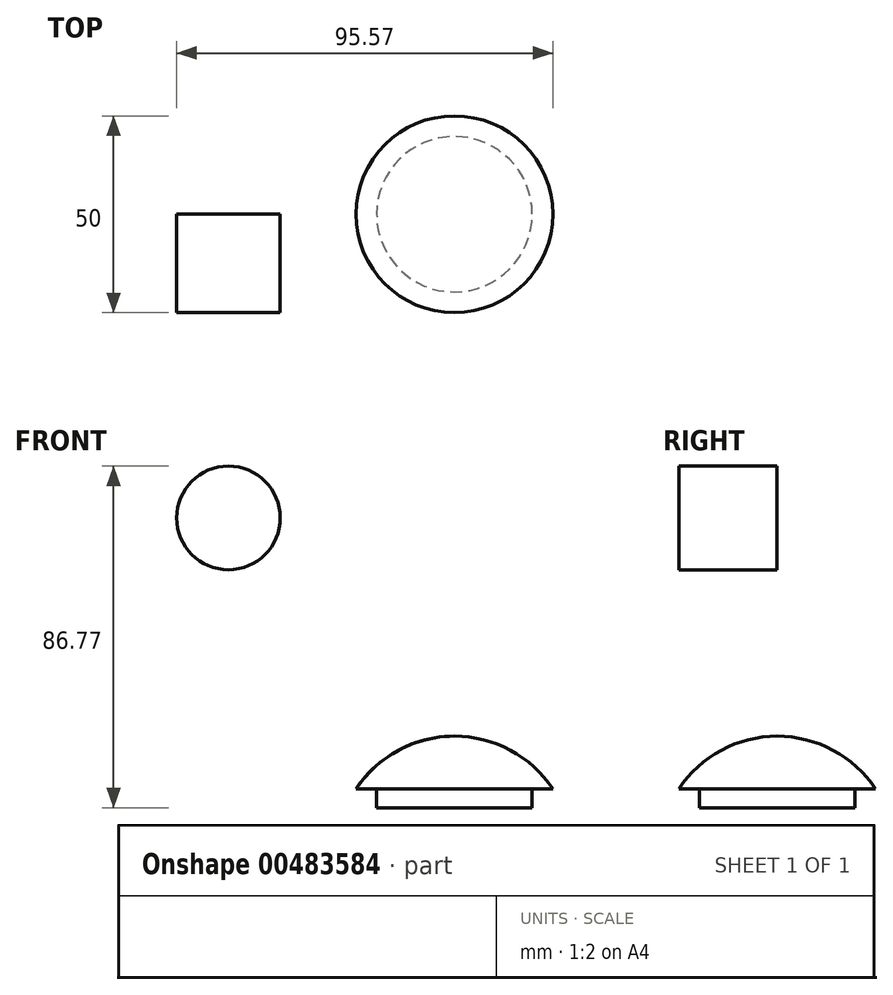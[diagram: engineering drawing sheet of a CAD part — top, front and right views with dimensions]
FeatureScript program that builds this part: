
annotation { "Feature Type Name" : "Feature", "Feature Type Description" : "" }
export const myFeature = defineFeature(function(context is Context, id is Id, definition is map)
    precondition{}
    {
        {
            var Q0;
            Q0=qCreatedBy(makeId("Top.planeOp"),FACE);
            var sketch = newSketch(context, id + "F0", { "sketchPlane" : qUnion([Q0])});
            skCircle(sketch, "E0", {"center": v(0, 0) * mm, "radius": 19.75 * mm});
            skSolve(sketch);
        }
        {
            var Q0;
            Q0=makeQuery(id+"F0.imprint","IMPRINT",FACE,{"disambiguationData":[TD([[makeQuery(id+"F0.imprint","IMPRINT",EDGE,{"derivedFrom":sQuery(id+"F0.wireOp",EDGE,"E0")}),1.0]])]});
            extrude(context, id + "F1", {"entities" : qUnion([Q0]), "oppositeDirection" : true, "depth" : 4.75 * mm});
        }
        {
            var Q0;
            Q0=qCreatedBy(makeId("Front.planeOp"),FACE);
            var sketch = newSketch(context, id + "F2", { "sketchPlane" : qUnion([Q0])});
            skLineSegment(sketch, "E1", {"start": v(0, 0) * mm, "end": v(-25, 0) * mm});
            skArc(sketch, "E2", {"start": v(0, 13.42) * mm, "mid": v(-14.19, 9.85) * mm, "end": v(-25, 0) * mm});
            skLineSegment(sketch, "E3", {"start": v(0, 13.42) * mm, "end": v(0, 0) * mm});
            skLineSegment(sketch, "E4", {"start": v(0, 13.42) * mm, "end": v(16.84, 13.42) * mm, "construction": true});
            skSolve(sketch);
        }
        {
            var Q0;
            Q0=makeQuery(id+"F2.imprint","IMPRINT",FACE,{"disambiguationData":[TD([[makeQuery(id+"F2.imprint","IMPRINT",EDGE,{"derivedFrom":sQuery(id+"F2.wireOp",EDGE,"E1")}),-1.0]])]});
            var Q1;
            Q1=sQuery(id+"F2.wireOp",EDGE,"E3");
            revolve(context, id + "F3", {"operationType" : NewBodyOperationType.ADD, "entities" : qUnion([Q0]), "axis" : qUnion([Q1]), "revolveType" : RevolveType.FULL});
        }
        {
            var Q0;
            Q0=qCreatedBy(makeId("Front.planeOp"),FACE);
            var sketch = newSketch(context, id + "F4", { "sketchPlane" : qUnion([Q0])});
            skCircle(sketch, "E5", {"center": v(-57.42, 68.86) * mm, "radius": 13.16 * mm});
            skSolve(sketch);
        }
        {
            var Q0;
            Q0=makeQuery(id+"F4.imprint","IMPRINT",FACE,{"disambiguationData":[TD([[makeQuery(id+"F4.imprint","IMPRINT",EDGE,{"derivedFrom":sQuery(id+"F4.wireOp",EDGE,"E5")}),1.0]])]});
            extrude(context, id + "F5", {"entities" : qUnion([Q0]), "depth" : 25 * mm});
        }
    });
